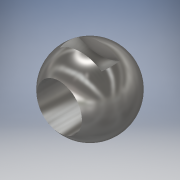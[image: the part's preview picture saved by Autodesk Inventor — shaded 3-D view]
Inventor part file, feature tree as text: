
AUTODESK INVENTOR PART (.ipt)
format: ipt  version: 2018 (Build 220112000, 112)  size: 154,624 bytes
history: native  units: mm
features: plane x3, sketch x2, revolve x1, extrude x1
ambient origin geometry x8: Origin, YZ Plane, XZ Plane, XY Plane, X Axis, Y Axis, Z Axis, Center Point
bodies: Solid1 (feature_tree)
feature tree (7):
  revolve  "Revolution1"  [1 undecoded]
  plane  "Work Plane5"
  plane  "Work Plane7"
  extrude  "Extrusion1"  TaperAngle=90.0deg  [1 undecoded]
  sketch  "Sketch1"  dims[d0=54.0mm d1=32.0mm]
  plane  "Work Plane6"
  sketch  "Sketch4"  dims[d2=27.0mm d3=90.0deg d10=50.0mm d11=32.0mm d12=10.171573mm d13=24.346814mm d14=0.0mm d15=13.0mm d16=0.0mm]
note: 2 required parameter values undecoded (feature->parameter linkage not recoverable at this tier; creation-order binding heuristic only, values carry confidence <= 0.55)